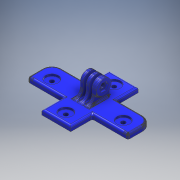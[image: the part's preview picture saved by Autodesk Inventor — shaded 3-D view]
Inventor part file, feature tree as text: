
AUTODESK INVENTOR PART (.ipt)
format: ipt  version: 2018 (Build 220112000, 112)  size: 4,092,416 bytes
history: native  units: mm
features: extrude x8, sketch x8, fillet x5, projected_geometry x5, imported_body x1
ambient origin geometry x8: Origin, YZ Plane, XZ Plane, XY Plane, X Axis, Y Axis, Z Axis, Center Point
bodies: Solid1 (feature_tree)
feature tree (27):
  extrude  "Extrusion1"  Depth=1.999mm
  fillet  "Fillet1"  Radius=4.3mm
  extrude  "Extrusion2"  Depth=1.6mm
  fillet  "Fillet2"  Radius=30.0mm
  extrude  "Extrusion3"  Depth=25.0mm
  extrude  "Extrusion4"  Depth=2.0mm
  fillet  "Fillet3"  Radius=4.5mm
  fillet  "Fillet4"  Radius=2.0mm
  fillet  "Fillet5"  Radius=2.0mm
  extrude  "Extrusion5"  Depth=0.25mm TaperAngle=0.0deg
  extrude  "Extrusion6"  Depth=0.25mm TaperAngle=0.0deg
  extrude  "Extrusion7"  [1 undecoded]
  extrude  "Extrusion8"  [1 undecoded]
  sketch  "Sketch1"  dims[d0=5.0mm d1=0.0mm d2=1.999mm d3=4.3mm]
  sketch  "Sketch2"  dims[d4=3.0mm d5=0.0mm d6=1.6mm d7=30.0mm]
  projected_geometry  "Projected Loop1"
  sketch  "Sketch3"  dims[d8=70.0mm d9=25.0mm]
  sketch  "Sketch4"  dims[d10=5.0mm d11=0.0mm d12=2.0mm d13=4.5mm d14=2.0mm d15=0.0mm d16=2.0mm]
  sketch  "Sketch5"  dims[d17=2.0mm d18=0.25mm d19=0.0mm]
  projected_geometry  "Projected Loop2"
  sketch  "Sketch6"  dims[d20=0.25mm d21=0.0mm d22=0.25mm d23=0.0mm]
  projected_geometry  "Projected Loop3"
  sketch  "Sketch7"  dims[d24=0.25mm d25=0.0mm]
  projected_geometry  "Projected Loop4"
  sketch  "Sketch8"
  projected_geometry  "Projected Loop5"
  imported_body  "Base1"
note: 2 required parameter values undecoded (feature->parameter linkage not recoverable at this tier; creation-order binding heuristic only, values carry confidence <= 0.55)
